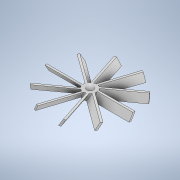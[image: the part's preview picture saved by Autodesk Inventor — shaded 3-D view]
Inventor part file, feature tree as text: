
AUTODESK INVENTOR PART (.ipt)
format: ipt  version: 2021 (Build 250183000, 183)  size: 164,864 bytes
history: native  units: mm
features: extrude x4, sketch x4, pattern_circular x1, fillet x1
ambient origin geometry x8: Origin, YZ Plane, XZ Plane, XY Plane, X Axis, Y Axis, Z Axis, Center Point
bodies: Solid1 (feature_tree)
feature tree (10):
  extrude  "Extrusion1"  Depth=10.0mm TaperAngle=0.0deg
  extrude  "Extrusion2"  Depth=10.0mm
  pattern_circular  "Circular Pattern1"  [2 undecoded]
  extrude  "Extrusion3"  Depth=2.0mm TaperAngle=0.0deg
  fillet  "Fillet1"  Radius=100.0mm
  extrude  "Extrusion4"  Depth=10.0mm
  sketch  "Sketch1"  dims[d0=20.0mm d1=10.0mm d2=0.0mm]
  sketch  "Sketch3"  dims[d3=3.0mm d4=10.0mm]
  sketch  "Sketch4"  dims[d5=10.0mm]
  sketch  "Sketch5"  dims[d6=60.0deg d7=5.0mm d8=63.5mm d9=0.0mm d10=100.0mm d11=360.0deg d13=10.0mm d14=5.0mm d15=0.0mm d16=5.0mm d17=5.0mm d18=2.0mm d19=0.0mm]
note: 2 required parameter values undecoded (feature->parameter linkage not recoverable at this tier; creation-order binding heuristic only, values carry confidence <= 0.55)
